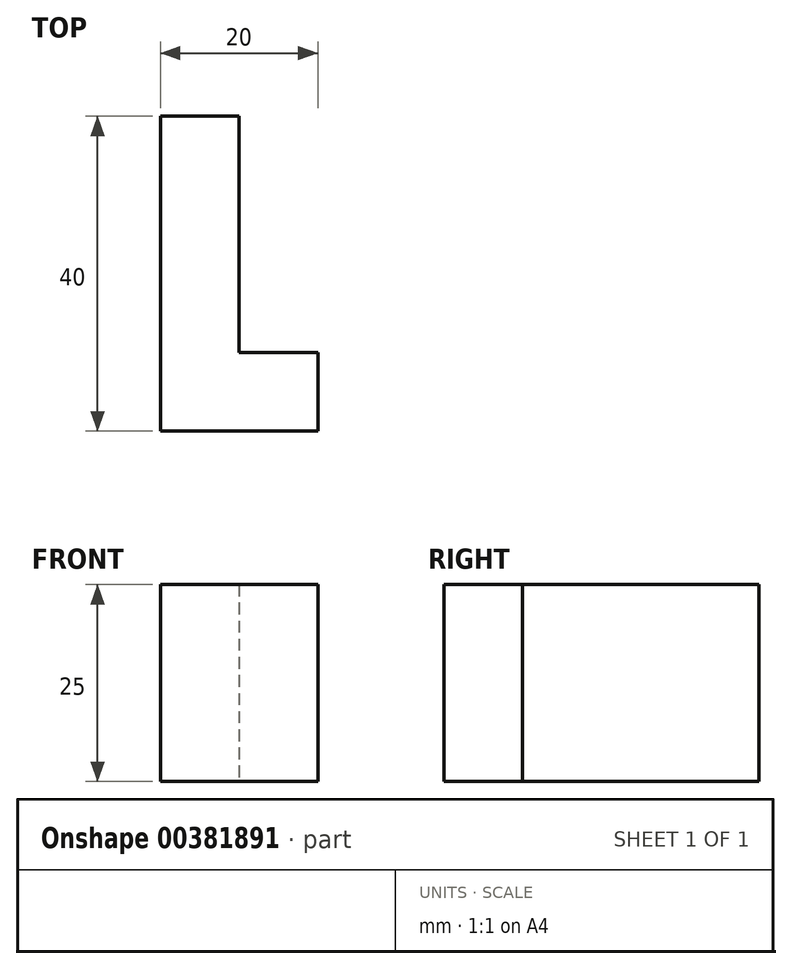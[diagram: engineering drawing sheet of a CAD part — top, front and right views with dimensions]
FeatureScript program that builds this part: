
annotation { "Feature Type Name" : "Feature", "Feature Type Description" : "" }
export const myFeature = defineFeature(function(context is Context, id is Id, definition is map)
    precondition{}
    {
        {
            var Q0;
            Q0=qCreatedBy(makeId("Top.planeOp"),FACE);
            var sketch = newSketch(context, id + "F0", { "sketchPlane" : qUnion([Q0])});
            skLineSegment(sketch, "E0", {"start": v(0, 0) * mm, "end": v(0, 40) * mm});
            skLineSegment(sketch, "E1", {"start": v(0, 40) * mm, "end": v(10, 40) * mm});
            skLineSegment(sketch, "E2", {"start": v(10, 40) * mm, "end": v(10, 10) * mm});
            skLineSegment(sketch, "E3", {"start": v(10, 10) * mm, "end": v(20, 10) * mm});
            skLineSegment(sketch, "E4", {"start": v(20, 10) * mm, "end": v(20, 0) * mm});
            skLineSegment(sketch, "E5", {"start": v(20, 0) * mm, "end": v(0, 0) * mm});
            skSolve(sketch);
        }
        {
            var Q0;
            Q0=makeQuery(id+"F0.imprint","IMPRINT",FACE,{"disambiguationData":[TD([[makeQuery(id+"F0.imprint","IMPRINT",EDGE,{"derivedFrom":sQuery(id+"F0.wireOp",EDGE,"E0")}),-1.0]])]});
            extrude(context, id + "F1", {"entities" : qUnion([Q0]), "depth" : 25 * mm});
        }
    });
